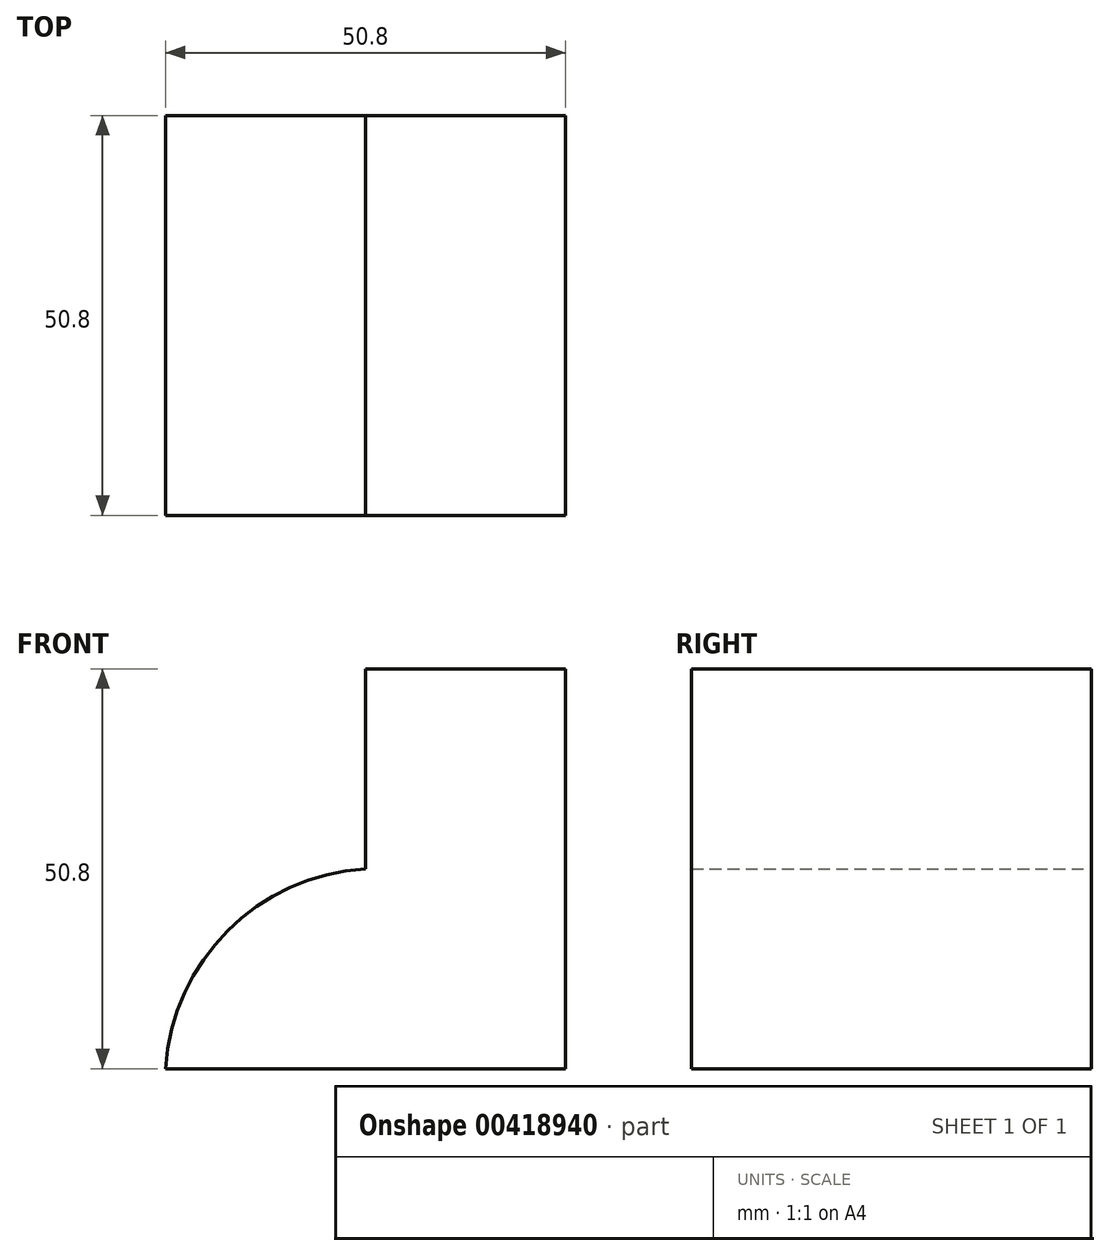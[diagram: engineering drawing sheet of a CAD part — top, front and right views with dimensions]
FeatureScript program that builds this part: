
annotation { "Feature Type Name" : "Feature", "Feature Type Description" : "" }
export const myFeature = defineFeature(function(context is Context, id is Id, definition is map)
    precondition{}
    {
        {
            var Q0;
            Q0=qCreatedBy(makeId("Front.planeOp"),FACE);
            var sketch = newSketch(context, id + "F0", { "sketchPlane" : qUnion([Q0])});
            skLineSegment(sketch, "E0", {"start": v(0, 0) * mm, "end": v(-50.8, 0) * mm});
            skLineSegment(sketch, "E1", {"start": v(0, 0) * mm, "end": v(0, 50.8) * mm});
            skLineSegment(sketch, "E2", {"start": v(0, 50.8) * mm, "end": v(-25.4, 50.8) * mm});
            skLineSegment(sketch, "E3", {"start": v(-25.4, 50.8) * mm, "end": v(-25.4, 25.4) * mm});
            skArc(sketch, "E4", {"start": v(-25.4, 25.4) * mm, "mid": v(-42.91, 17.51) * mm, "end": v(-50.8, 0) * mm});
            skSolve(sketch);
        }
        {
            var Q0;
            Q0 = qSketchRegion(id + "F0", true);
            extrude(context, id + "F1", {"entities" : qUnion([Q0]), "depth" : 50.8 * mm});
        }
    });
